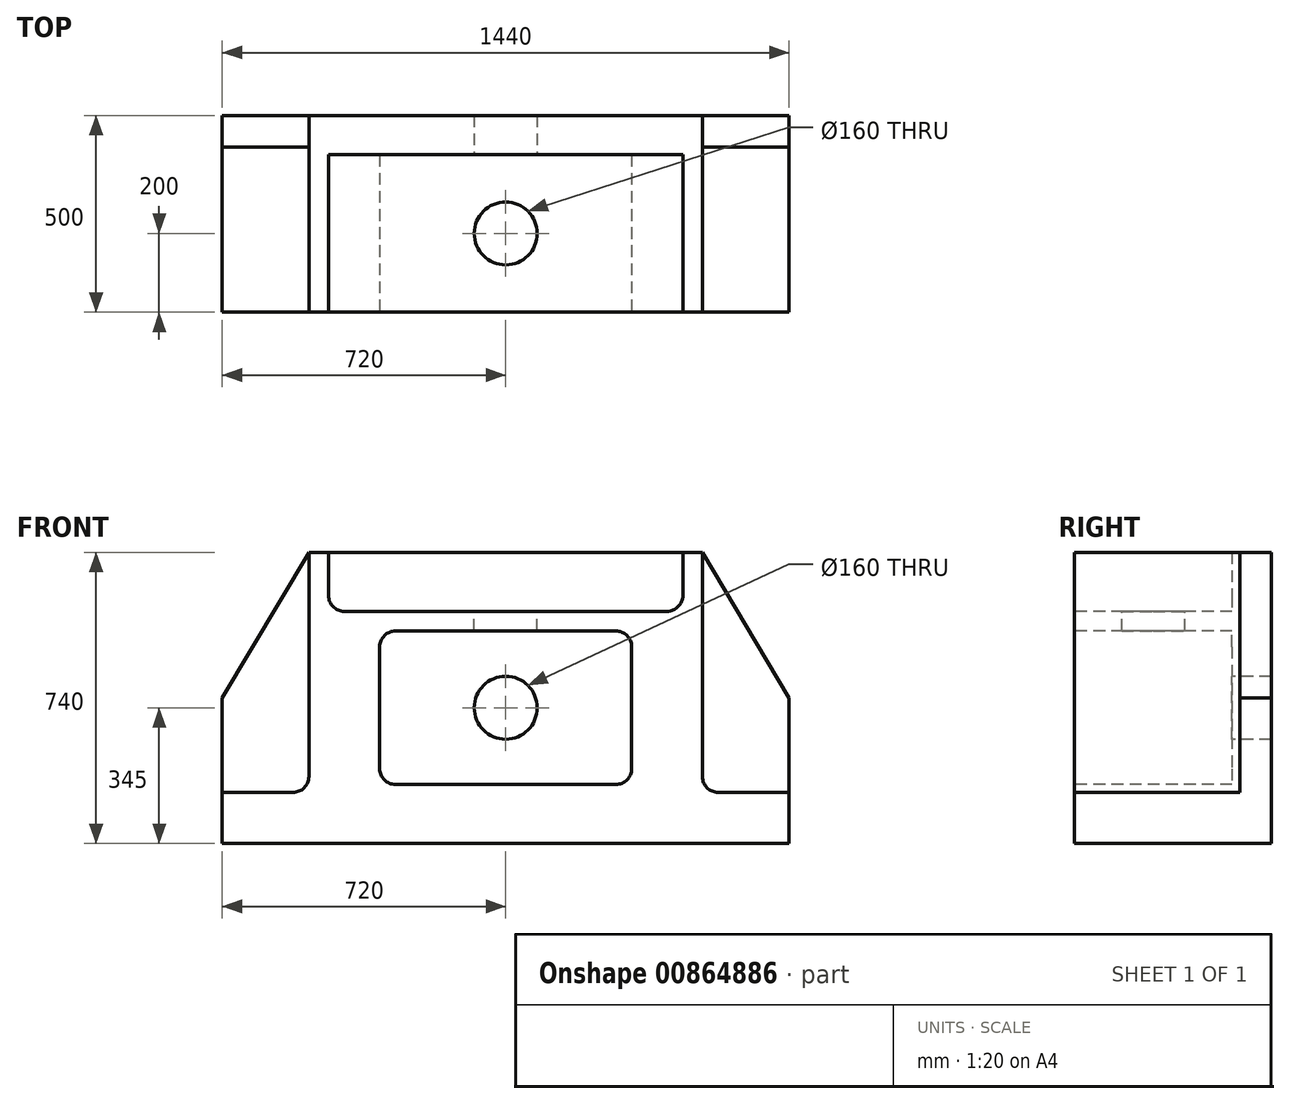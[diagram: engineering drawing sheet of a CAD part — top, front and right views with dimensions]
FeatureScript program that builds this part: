
annotation { "Feature Type Name" : "Feature", "Feature Type Description" : "" }
export const myFeature = defineFeature(function(context is Context, id is Id, definition is map)
    precondition{}
    {
        {
            var Q0;
            Q0=qCreatedBy(makeId("Front.planeOp"),FACE);
            var sketch = newSketch(context, id + "F0", { "sketchPlane" : qUnion([Q0])});
            skLineSegment(sketch, "E0.bottom", {"start": v(500, 370) * mm, "end": v(-500, 370) * mm});
            skLineSegment(sketch, "E0.top", {"start": v(500, -370) * mm, "end": v(-500, -370) * mm});
            skLineSegment(sketch, "E0.left", {"start": v(500, 370) * mm, "end": v(500, -370) * mm});
            skLineSegment(sketch, "E0.right", {"start": v(-500, 370) * mm, "end": v(-500, -370) * mm});
            skPoint(sketch, "E0.middle", {"position": v(0, 0) * mm});
            skSolve(sketch);
        }
        {
            var Q0;
            Q0 = qSketchRegion(id + "F0", true);
            extrude(context, id + "F1", {"entities" : qUnion([Q0]), "depth" : 500 * mm, "offsetDistance" : 25 * mm});
        }
        {
            var Q0;
            Q0=makeQuery(id+"F1.opExtrude","CAP_FACE",FACE,{"disambiguationData":[OSD([sQuery(id+"F0.wireOp",EDGE,"E0.bottom"),sQuery(id+"F0.wireOp",EDGE,"E0.top"),sQuery(id+"F0.wireOp",EDGE,"E0.left"),sQuery(id+"F0.wireOp",EDGE,"E0.right")])],"isStart":false});
            var sketch = newSketch(context, id + "F2", { "sketchPlane" : qUnion([Q0])});
            skLineSegment(sketch, "E1.bottom", {"start": v(280, 170) * mm, "end": v(-280, 170) * mm});
            skLineSegment(sketch, "E1.top", {"start": v(280, -220) * mm, "end": v(-280, -220) * mm});
            skLineSegment(sketch, "E1.left", {"start": v(320, 130) * mm, "end": v(320, -180) * mm});
            skLineSegment(sketch, "E1.right", {"start": v(-320, 130) * mm, "end": v(-320, -180) * mm});
            skPoint(sketch, "E1.middle", {"position": v(0, -25) * mm});
            skPoint(sketch, "E2.visualSharp", {"position": v(-320, 170) * mm});
            skArc(sketch, "E2.filletArc", {"start": v(-280, 170) * mm, "mid": v(-308.28, 158.28) * mm, "end": v(-320, 130) * mm});
            skPoint(sketch, "E3.visualSharp", {"position": v(-320, -220) * mm});
            skArc(sketch, "E3.filletArc", {"start": v(-320, -180) * mm, "mid": v(-308.28, -208.28) * mm, "end": v(-280, -220) * mm});
            skPoint(sketch, "E4.visualSharp", {"position": v(320, -220) * mm});
            skArc(sketch, "E4.filletArc", {"start": v(280, -220) * mm, "mid": v(308.28, -208.28) * mm, "end": v(320, -180) * mm});
            skPoint(sketch, "E5.visualSharp", {"position": v(320, 170) * mm});
            skArc(sketch, "E5.filletArc", {"start": v(320, 130) * mm, "mid": v(308.28, 158.28) * mm, "end": v(280, 170) * mm});
            skSolve(sketch);
        }
        {
            var Q0;
            Q0 = qSketchRegion(id + "F2", true);
            extrude(context, id + "F3", {"entities" : qUnion([Q0]), "operationType" : NewBodyOperationType.REMOVE, "oppositeDirection" : true, "depth" : 400 * mm, "offsetDistance" : 25 * mm});
        }
        {
            var Q0;
            Q0=makeQuery(id+"F3.boolean.opBoolean","COPY",FACE,{"derivedFrom":makeQuery(id+"F3.opExtrude","CAP_FACE",FACE,{"disambiguationData":[OSD([sQuery(id+"F2.wireOp",EDGE,"E1.bottom"),sQuery(id+"F2.wireOp",EDGE,"E1.top"),sQuery(id+"F2.wireOp",EDGE,"E1.left"),sQuery(id+"F2.wireOp",EDGE,"E1.right"),sQuery(id+"F2.wireOp",EDGE,"E2.filletArc"),sQuery(id+"F2.wireOp",EDGE,"E3.filletArc"),sQuery(id+"F2.wireOp",EDGE,"E4.filletArc"),sQuery(id+"F2.wireOp",EDGE,"E5.filletArc")])],"isStart":false})});
            var sketch = newSketch(context, id + "F4", { "sketchPlane" : qUnion([Q0])});
            skCircle(sketch, "E6", {"center": v(0, -25) * mm, "radius": 80 * mm});
            skPoint(sketch, "E6.centerSnap0", {"position": v(320, -25) * mm});
            skSolve(sketch);
        }
        {
            var Q0;
            Q0 = qSketchRegion(id + "F4", true);
            extrude(context, id + "F5", {"entities" : qUnion([Q0]), "operationType" : NewBodyOperationType.REMOVE, "endBound" : BoundingType.THROUGH_ALL, "oppositeDirection" : true, "depth" : 25 * mm, "offsetDistance" : 25 * mm});
        }
        {
            var Q0;
            Q0=makeQuery(id+"F1.opExtrude","CAP_FACE",FACE,{"disambiguationData":[OSD([sQuery(id+"F0.wireOp",EDGE,"E0.bottom"),sQuery(id+"F0.wireOp",EDGE,"E0.top"),sQuery(id+"F0.wireOp",EDGE,"E0.left"),sQuery(id+"F0.wireOp",EDGE,"E0.right")])],"isStart":false});
            var sketch = newSketch(context, id + "F6", { "sketchPlane" : qUnion([Q0])});
            skLineSegment(sketch, "E7.bottom", {"start": v(450, 520) * mm, "end": v(-450, 520) * mm});
            skLineSegment(sketch, "E7.top", {"start": v(410, 220) * mm, "end": v(-410, 220) * mm});
            skLineSegment(sketch, "E7.left", {"start": v(450, 520) * mm, "end": v(450, 260) * mm});
            skLineSegment(sketch, "E7.right", {"start": v(-450, 520) * mm, "end": v(-450, 260) * mm});
            skPoint(sketch, "E7.middle", {"position": v(0, 370) * mm});
            skPoint(sketch, "E8.visualSharp", {"position": v(-450, 220) * mm});
            skArc(sketch, "E8.filletArc", {"start": v(-450, 260) * mm, "mid": v(-438.28, 231.72) * mm, "end": v(-410, 220) * mm});
            skPoint(sketch, "E9.visualSharp", {"position": v(450, 220) * mm});
            skArc(sketch, "E9.filletArc", {"start": v(410, 220) * mm, "mid": v(438.28, 231.72) * mm, "end": v(450, 260) * mm});
            skSolve(sketch);
        }
        {
            var Q0;
            Q0 = qSketchRegion(id + "F6", true);
            extrude(context, id + "F7", {"entities" : qUnion([Q0]), "operationType" : NewBodyOperationType.REMOVE, "oppositeDirection" : true, "depth" : 400 * mm, "offsetDistance" : 25 * mm});
        }
        {
            var Q0;
            Q0=makeQuery(id+"F1.opExtrude","SWEPT_FACE",FACE,{"disambiguationData":[OSD([sQuery(id+"F0.wireOp",EDGE,"E0.left")])]});
            var sketch = newSketch(context, id + "F8", { "sketchPlane" : qUnion([Q0])});
            skLineSegment(sketch, "E10.bottom", {"start": v(-500, -370) * mm, "end": v(0, -370) * mm});
            skLineSegment(sketch, "E10.top", {"start": v(-500, -240) * mm, "end": v(0, -240) * mm});
            skLineSegment(sketch, "E10.left", {"start": v(-500, -370) * mm, "end": v(-500, -240) * mm});
            skLineSegment(sketch, "E10.right", {"start": v(0, -370) * mm, "end": v(0, -240) * mm});
            skSolve(sketch);
        }
        {
            var Q0;
            Q0 = qSketchRegion(id + "F8", true);
            extrude(context, id + "F9", {"entities" : qUnion([Q0]), "operationType" : NewBodyOperationType.ADD, "depth" : 220 * mm, "offsetDistance" : 25 * mm});
        }
        {
            var Q0;
            Q0=makeQuery(id+"F1.opExtrude","SWEPT_FACE",FACE,{"disambiguationData":[OSD([sQuery(id+"F0.wireOp",EDGE,"E0.right")])]});
            var sketch = newSketch(context, id + "F10", { "sketchPlane" : qUnion([Q0])});
            skLineSegment(sketch, "E11.bottom", {"start": v(0, -370) * mm, "end": v(500, -370) * mm});
            skLineSegment(sketch, "E11.top", {"start": v(0, -240) * mm, "end": v(500, -240) * mm});
            skLineSegment(sketch, "E11.left", {"start": v(0, -370) * mm, "end": v(0, -240) * mm});
            skLineSegment(sketch, "E11.right", {"start": v(500, -370) * mm, "end": v(500, -240) * mm});
            skSolve(sketch);
        }
        {
            var Q0;
            Q0 = qSketchRegion(id + "F10", true);
            extrude(context, id + "F11", {"entities" : qUnion([Q0]), "operationType" : NewBodyOperationType.ADD, "depth" : 220 * mm, "offsetDistance" : 25 * mm});
        }
        {
            var Q0;
            Q0=makeQuery(id+"F1.opExtrude","SWEPT_FACE",FACE,{"disambiguationData":[OSD([sQuery(id+"F0.wireOp",EDGE,"E0.right")])]});
            var sketch = newSketch(context, id + "F12", { "sketchPlane" : qUnion([Q0])});
            skLineSegment(sketch, "E12.bottom", {"start": v(0, -240) * mm, "end": v(500, -240) * mm});
            skLineSegment(sketch, "E12.top", {"start": v(0, 370) * mm, "end": v(500, 370) * mm});
            skLineSegment(sketch, "E12.left", {"start": v(0, -240) * mm, "end": v(0, 370) * mm});
            skLineSegment(sketch, "E12.right", {"start": v(500, -240) * mm, "end": v(500, 370) * mm});
            skSolve(sketch);
        }
        {
            var Q0;
            Q0 = qSketchRegion(id + "F12", true);
            extrude(context, id + "F13", {"entities" : qUnion([Q0]), "operationType" : NewBodyOperationType.ADD, "depth" : 220 * mm, "offsetDistance" : 25 * mm});
        }
        {
            var Q0;
            Q0=makeQuery(id+"F13.boolean.opBoolean","MERGE",FACE,{"derivedFrom":[makeQuery(id+"F11.boolean.opBoolean","MERGE",FACE,{"derivedFrom":[makeQuery(id+"F9.boolean.opBoolean","MERGE",FACE,{"derivedFrom":[makeQuery(id+"F1.opExtrude","CAP_FACE",FACE,{"disambiguationData":[OSD([sQuery(id+"F0.wireOp",EDGE,"E0.bottom"),sQuery(id+"F0.wireOp",EDGE,"E0.top"),sQuery(id+"F0.wireOp",EDGE,"E0.left"),sQuery(id+"F0.wireOp",EDGE,"E0.right")])],"isStart":false}),makeQuery(id+"F9.opExtrude","SWEPT_FACE",FACE,{"disambiguationData":[OSD([sQuery(id+"F8.wireOp",EDGE,"E10.left")])]})]}),makeQuery(id+"F11.opExtrude","SWEPT_FACE",FACE,{"disambiguationData":[OSD([sQuery(id+"F10.wireOp",EDGE,"E11.right")])]})]}),makeQuery(id+"F13.opExtrude","SWEPT_FACE",FACE,{"disambiguationData":[OSD([sQuery(id+"F12.wireOp",EDGE,"E12.right")])]})]});
            var sketch = newSketch(context, id + "F14", { "sketchPlane" : qUnion([Q0])});
            skPoint(sketch, "E13", {"position": v(-720, 0) * mm});
            skPoint(sketch, "E14", {"position": v(-500, 370) * mm});
            skLineSegment(sketch, "E15", {"start": v(-720, 0) * mm, "end": v(-500, 370) * mm});
            skLineSegment(sketch, "E16", {"start": v(-720, 0) * mm, "end": v(-720, 370) * mm});
            skLineSegment(sketch, "E17", {"start": v(-720, 370) * mm, "end": v(-500, 370) * mm});
            skSolve(sketch);
        }
        {
            var Q0;
            Q0 = qSketchRegion(id + "F14", true);
            extrude(context, id + "F15", {"entities" : qUnion([Q0]), "operationType" : NewBodyOperationType.REMOVE, "endBound" : BoundingType.THROUGH_ALL, "oppositeDirection" : true, "depth" : 25 * mm, "offsetDistance" : 25 * mm});
        }
        {
            var Q0;
            Q0=makeQuery(id+"F13.boolean.opBoolean","MERGE",FACE,{"derivedFrom":[makeQuery(id+"F11.boolean.opBoolean","MERGE",FACE,{"derivedFrom":[makeQuery(id+"F9.boolean.opBoolean","MERGE",FACE,{"derivedFrom":[makeQuery(id+"F1.opExtrude","CAP_FACE",FACE,{"disambiguationData":[OSD([sQuery(id+"F0.wireOp",EDGE,"E0.bottom"),sQuery(id+"F0.wireOp",EDGE,"E0.top"),sQuery(id+"F0.wireOp",EDGE,"E0.left"),sQuery(id+"F0.wireOp",EDGE,"E0.right")])],"isStart":false}),makeQuery(id+"F9.opExtrude","SWEPT_FACE",FACE,{"disambiguationData":[OSD([sQuery(id+"F8.wireOp",EDGE,"E10.left")])]})]}),makeQuery(id+"F11.opExtrude","SWEPT_FACE",FACE,{"disambiguationData":[OSD([sQuery(id+"F10.wireOp",EDGE,"E11.right")])]})]}),makeQuery(id+"F13.opExtrude","SWEPT_FACE",FACE,{"disambiguationData":[OSD([sQuery(id+"F12.wireOp",EDGE,"E12.right")])]})]});
            var sketch = newSketch(context, id + "F16", { "sketchPlane" : qUnion([Q0])});
            skLineSegment(sketch, "E18", {"start": v(-500, 370) * mm, "end": v(-500, -240) * mm});
            skLineSegment(sketch, "E19", {"start": v(-500, -240) * mm, "end": v(-720, -240) * mm});
            skLineSegment(sketch, "E20", {"start": v(-720, -240) * mm, "end": v(-720, 0) * mm});
            skLineSegment(sketch, "E21", {"start": v(-720, 0) * mm, "end": v(-500, 370) * mm});
            skSolve(sketch);
        }
        {
            var Q0;
            Q0 = qSketchRegion(id + "F16", true);
            extrude(context, id + "F17", {"entities" : qUnion([Q0]), "operationType" : NewBodyOperationType.REMOVE, "oppositeDirection" : true, "depth" : 420 * mm, "offsetDistance" : 25 * mm});
        }
        {
            var Q0;
            Q0=makeQuery(id+"F1.opExtrude","SWEPT_FACE",FACE,{"disambiguationData":[OSD([sQuery(id+"F0.wireOp",EDGE,"E0.left")])]});
            var sketch = newSketch(context, id + "F18", { "sketchPlane" : qUnion([Q0])});
            skLineSegment(sketch, "E22.bottom", {"start": v(-500, -240) * mm, "end": v(0, -240) * mm});
            skLineSegment(sketch, "E22.top", {"start": v(-500, 370) * mm, "end": v(0, 370) * mm});
            skLineSegment(sketch, "E22.left", {"start": v(-500, -240) * mm, "end": v(-500, 370) * mm});
            skLineSegment(sketch, "E22.right", {"start": v(0, -240) * mm, "end": v(0, 370) * mm});
            skSolve(sketch);
        }
        {
            var Q0;
            Q0 = qSketchRegion(id + "F18", true);
            extrude(context, id + "F19", {"entities" : qUnion([Q0]), "operationType" : NewBodyOperationType.ADD, "depth" : 220 * mm, "offsetDistance" : 25 * mm});
        }
        {
            var Q0;
            Q0=makeQuery(id+"F19.boolean.opBoolean","MERGE",FACE,{"derivedFrom":[makeQuery(id+"F13.boolean.opBoolean","MERGE",FACE,{"derivedFrom":[makeQuery(id+"F11.boolean.opBoolean","MERGE",FACE,{"derivedFrom":[makeQuery(id+"F9.boolean.opBoolean","MERGE",FACE,{"derivedFrom":[makeQuery(id+"F1.opExtrude","CAP_FACE",FACE,{"disambiguationData":[OSD([sQuery(id+"F0.wireOp",EDGE,"E0.bottom"),sQuery(id+"F0.wireOp",EDGE,"E0.top"),sQuery(id+"F0.wireOp",EDGE,"E0.left"),sQuery(id+"F0.wireOp",EDGE,"E0.right")])],"isStart":false}),makeQuery(id+"F9.opExtrude","SWEPT_FACE",FACE,{"disambiguationData":[OSD([sQuery(id+"F8.wireOp",EDGE,"E10.left")])]})]}),makeQuery(id+"F11.opExtrude","SWEPT_FACE",FACE,{"disambiguationData":[OSD([sQuery(id+"F10.wireOp",EDGE,"E11.right")])]})]}),makeQuery(id+"F13.opExtrude","SWEPT_FACE",FACE,{"disambiguationData":[OSD([sQuery(id+"F12.wireOp",EDGE,"E12.right")])]})]}),makeQuery(id+"F19.opExtrude","SWEPT_FACE",FACE,{"disambiguationData":[OSD([sQuery(id+"F18.wireOp",EDGE,"E22.left")])]})]});
            var sketch = newSketch(context, id + "F20", { "sketchPlane" : qUnion([Q0])});
            skPoint(sketch, "E23", {"position": v(720, 0) * mm});
            skPoint(sketch, "E24", {"position": v(500, 370) * mm});
            skLineSegment(sketch, "E25", {"start": v(500, 370) * mm, "end": v(720, 370) * mm});
            skLineSegment(sketch, "E26", {"start": v(720, 370) * mm, "end": v(720, 0) * mm});
            skLineSegment(sketch, "E27", {"start": v(720, 0) * mm, "end": v(500, 370) * mm});
            skSolve(sketch);
        }
        {
            var Q0;
            Q0 = qSketchRegion(id + "F20", true);
            extrude(context, id + "F21", {"entities" : qUnion([Q0]), "operationType" : NewBodyOperationType.REMOVE, "endBound" : BoundingType.THROUGH_ALL, "oppositeDirection" : true, "depth" : 25 * mm, "offsetDistance" : 25 * mm});
        }
        {
            var Q0;
            Q0=makeQuery(id+"F19.boolean.opBoolean","MERGE",FACE,{"derivedFrom":[makeQuery(id+"F13.boolean.opBoolean","MERGE",FACE,{"derivedFrom":[makeQuery(id+"F11.boolean.opBoolean","MERGE",FACE,{"derivedFrom":[makeQuery(id+"F9.boolean.opBoolean","MERGE",FACE,{"derivedFrom":[makeQuery(id+"F1.opExtrude","CAP_FACE",FACE,{"disambiguationData":[OSD([sQuery(id+"F0.wireOp",EDGE,"E0.bottom"),sQuery(id+"F0.wireOp",EDGE,"E0.top"),sQuery(id+"F0.wireOp",EDGE,"E0.left"),sQuery(id+"F0.wireOp",EDGE,"E0.right")])],"isStart":false}),makeQuery(id+"F9.opExtrude","SWEPT_FACE",FACE,{"disambiguationData":[OSD([sQuery(id+"F8.wireOp",EDGE,"E10.left")])]})]}),makeQuery(id+"F11.opExtrude","SWEPT_FACE",FACE,{"disambiguationData":[OSD([sQuery(id+"F10.wireOp",EDGE,"E11.right")])]})]}),makeQuery(id+"F13.opExtrude","SWEPT_FACE",FACE,{"disambiguationData":[OSD([sQuery(id+"F12.wireOp",EDGE,"E12.right")])]})]}),makeQuery(id+"F19.opExtrude","SWEPT_FACE",FACE,{"disambiguationData":[OSD([sQuery(id+"F18.wireOp",EDGE,"E22.left")])]})]});
            var sketch = newSketch(context, id + "F22", { "sketchPlane" : qUnion([Q0])});
            skLineSegment(sketch, "E28", {"start": v(500, 370) * mm, "end": v(500, -240) * mm});
            skLineSegment(sketch, "E29", {"start": v(500, -240) * mm, "end": v(720, -240) * mm});
            skLineSegment(sketch, "E30", {"start": v(720, -240) * mm, "end": v(720, 0) * mm});
            skLineSegment(sketch, "E31", {"start": v(720, 0) * mm, "end": v(500, 370) * mm});
            skSolve(sketch);
        }
        {
            var Q0;
            Q0 = qSketchRegion(id + "F22", true);
            extrude(context, id + "F23", {"entities" : qUnion([Q0]), "operationType" : NewBodyOperationType.REMOVE, "oppositeDirection" : true, "depth" : 420 * mm, "offsetDistance" : 25 * mm});
        }
        {
            var Q0;
            Q0=makeQuery(id+"F7.boolean.opBoolean","COPY",FACE,{"derivedFrom":makeQuery(id+"F7.opExtrude","SWEPT_FACE",FACE,{"disambiguationData":[OSD([sQuery(id+"F6.wireOp",EDGE,"E7.top")])]})});
            var sketch = newSketch(context, id + "F24", { "sketchPlane" : qUnion([Q0])});
            skCircle(sketch, "E32", {"center": v(0, -300) * mm, "radius": 80 * mm});
            skPoint(sketch, "E32.centerSnap0", {"position": v(410, -300) * mm});
            skPoint(sketch, "E32.centerSnap1", {"position": v(0, -100) * mm});
            skSolve(sketch);
        }
        {
            var Q0;
            Q0 = qSketchRegion(id + "F24", true);
            extrude(context, id + "F25", {"entities" : qUnion([Q0]), "operationType" : NewBodyOperationType.REMOVE, "oppositeDirection" : true, "depth" : 50 * mm, "offsetDistance" : 25 * mm});
        }
        {
            var Q0;
            Q0=makeQuery(id+"F17.boolean.opBoolean","COPY",EDGE,{"derivedFrom":makeQuery(id+"F17.opExtrude","SWEPT_EDGE",EDGE,{"disambiguationData":[OSD([sQuery(id+"F16.wireOp",EDGE,"E18"),sQuery(id+"F16.wireOp",EDGE,"E19")])]})});
            var Q1;
            Q1=makeQuery(id+"F23.boolean.opBoolean","COPY",EDGE,{"derivedFrom":makeQuery(id+"F23.opExtrude","SWEPT_EDGE",EDGE,{"disambiguationData":[OSD([sQuery(id+"F22.wireOp",EDGE,"E28"),sQuery(id+"F22.wireOp",EDGE,"E29")])]})});
            fillet(context, id + "F26", {"entities" : qUnion([Q0, Q1]), "radius" : 40 * mm, "tangentPropagation" : true, "allowEdgeOverflow" : false});
        }
    });
